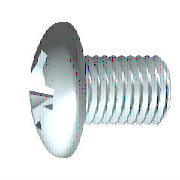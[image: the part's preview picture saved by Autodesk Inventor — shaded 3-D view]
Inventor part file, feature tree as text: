
AUTODESK INVENTOR PART (.ipt)
format: ipt  version: 2015 (Build 190159000, 159)  size: 329,728 bytes
history: native  units: mm (DEFAULTED — no unit token found)
features: other x2, extrude x2, plane x1
ambient origin geometry x7: Origin, YZ Plane, XZ Plane, X Axis, Y Axis, Z Axis, Center Point
bodies: Solid1 (feature_tree), Body (feature_tree)
feature tree (5):
  other  "IDS_WORKPLANE{1}"
  extrude  "Slot"  Depth=3.5mm
  other  "Cut"
  extrude  "Star Cut"  Depth=2.36mm
  plane  "Work Plane3"
